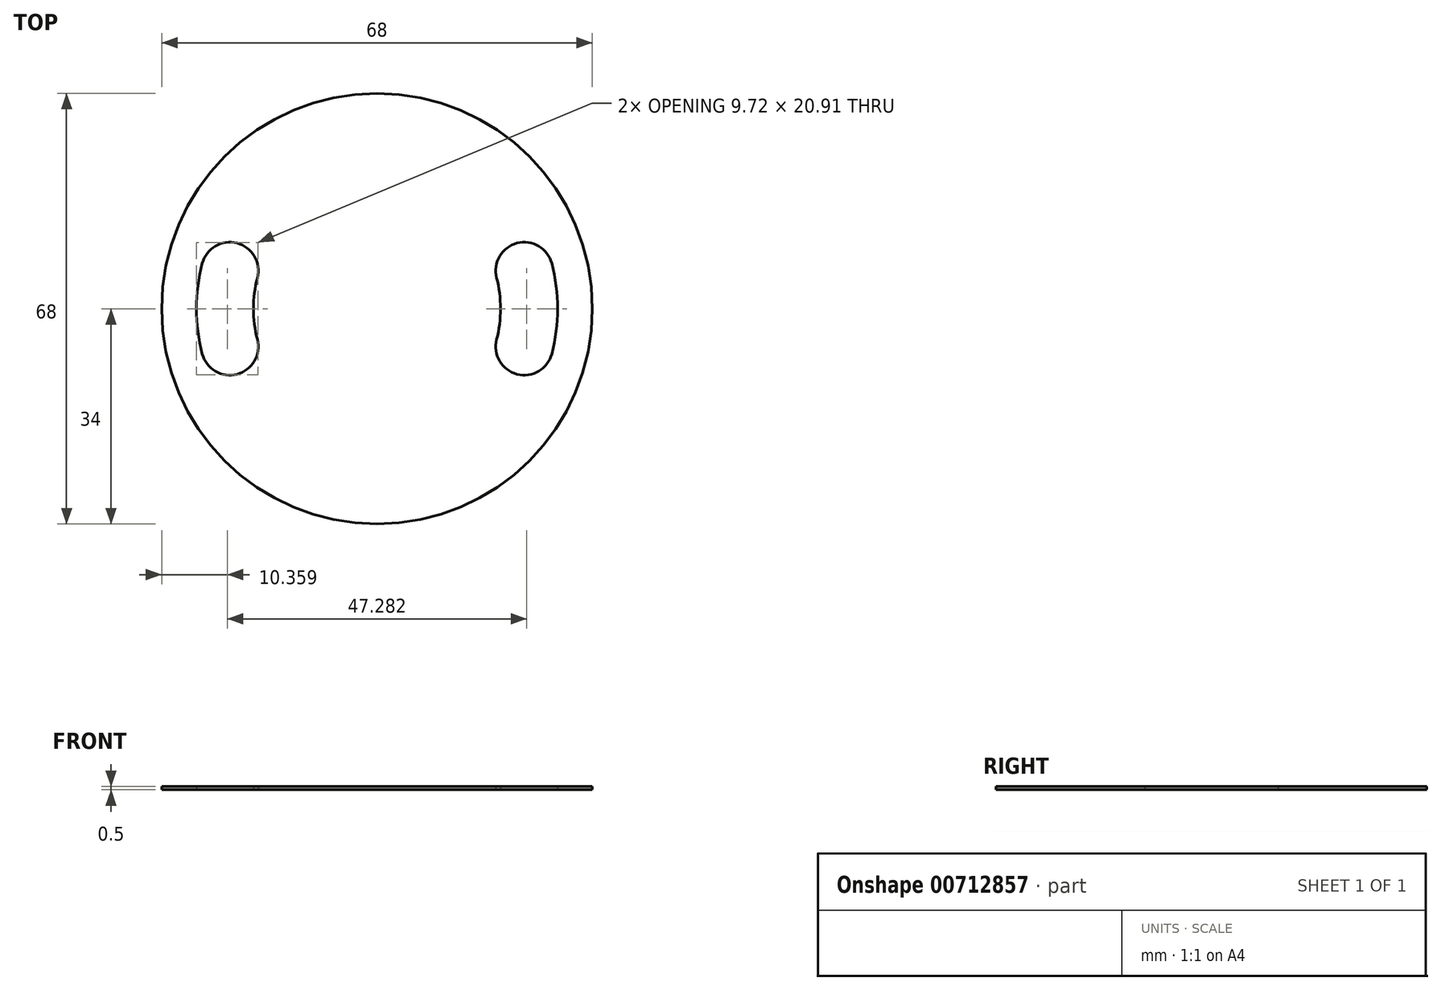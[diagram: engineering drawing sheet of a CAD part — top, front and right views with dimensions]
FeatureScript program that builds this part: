
annotation { "Feature Type Name" : "Feature", "Feature Type Description" : "" }
export const myFeature = defineFeature(function(context is Context, id is Id, definition is map)
    precondition{}
    {
        {
            var Q0;
            Q0=qCreatedBy(makeId("Top.planeOp"),FACE);
            var sketch = newSketch(context, id + "F0", { "sketchPlane" : qUnion([Q0])});
            skCircle(sketch, "E0", {"center": v(0, 0) * mm, "radius": 34 * mm});
            skArc(sketch, "E1", {"start": v(-18.88, 4.88) * mm, "mid": v(-22.11, 10.36) * mm, "end": v(-27.6, 7.13) * mm});
            skArc(sketch, "E2.MirrorC", {"start": v(-18.88, -4.88) * mm, "mid": v(-22.11, -10.36) * mm, "end": v(-27.6, -7.13) * mm});
            skArc(sketch, "E3", {"start": v(-18.88, 4.88) * mm, "mid": v(-19.5, 0) * mm, "end": v(-18.88, -4.88) * mm});
            skArc(sketch, "E4", {"start": v(-27.6, 7.12) * mm, "mid": v(-28.5, 0) * mm, "end": v(-27.6, -7.12) * mm});
            skArc(sketch, "E5", {"start": v(-21.7, 10.23) * mm, "mid": v(-24, 0) * mm, "end": v(-21.7, -10.23) * mm, "construction": true});
            skArc(sketch, "E6.MirrorCS", {"start": v(18.88, 4.88) * mm, "mid": v(22.11, 10.36) * mm, "end": v(27.6, 7.13) * mm});
            skArc(sketch, "E7.MirrorCS", {"start": v(27.6, 7.12) * mm, "mid": v(28.5, 0) * mm, "end": v(27.6, -7.12) * mm});
            skArc(sketch, "E8.MirrorCS", {"start": v(18.88, -4.88) * mm, "mid": v(22.11, -10.36) * mm, "end": v(27.6, -7.13) * mm});
            skArc(sketch, "E9.MirrorCS", {"start": v(18.88, 4.88) * mm, "mid": v(19.5, 0) * mm, "end": v(18.88, -4.88) * mm});
            skSolve(sketch);
        }
        {
            var Q0;
            Q0 = qSketchRegion(id + "F0", true);
            extrude(context, id + "F1", {"entities" : qUnion([Q0]), "depth" : 0.5 * mm, "offsetDistance" : 25 * mm});
        }
    });
